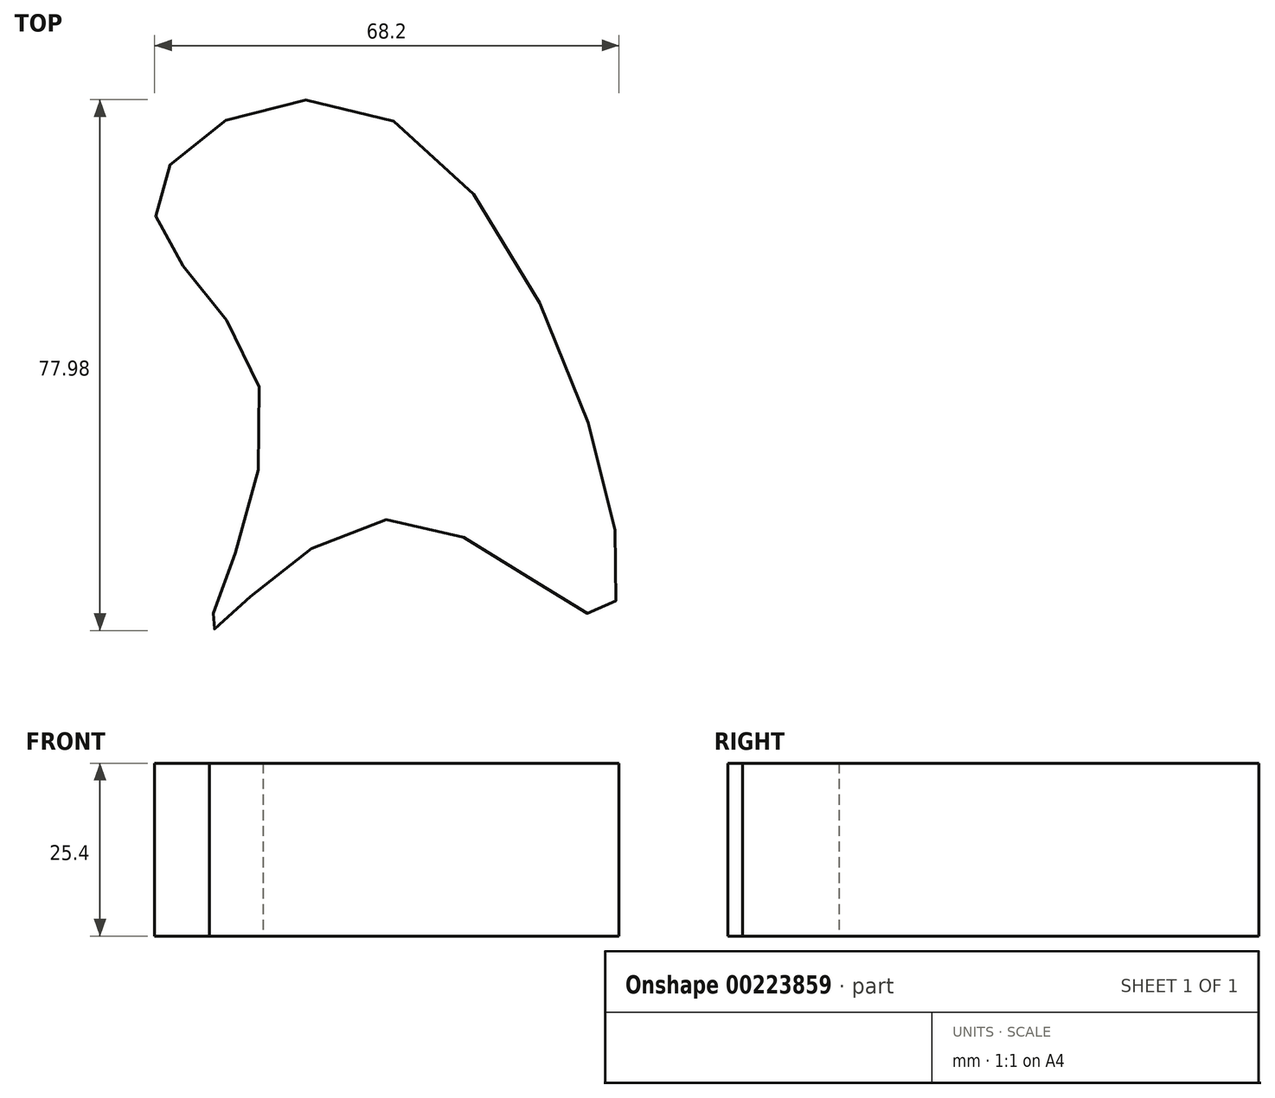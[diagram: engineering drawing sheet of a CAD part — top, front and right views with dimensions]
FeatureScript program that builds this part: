
annotation { "Feature Type Name" : "Feature", "Feature Type Description" : "" }
export const myFeature = defineFeature(function(context is Context, id is Id, definition is map)
    precondition{}
    {
        {
            var Q0;
            Q0=qCreatedBy(makeId("Top.planeOp"),FACE);
            var sketch = newSketch(context, id + "F0", { "sketchPlane" : qUnion([Q0])});
            skFitSpline(sketch, "E0", {"points": [v(0, 40.57) * mm, v(-35.01, 29.09) * mm, v(-19.45, 0) * mm, v(-26.86, -34.27) * mm, v(0, -17.97) * mm, v(31.68, -31.68) * mm, v(0, 40.57) * mm]});
            skSolve(sketch);
        }
        {
            var Q0;
            Q0 = qSketchRegion(id + "F0", true);
            extrude(context, id + "F1", {"entities" : qUnion([Q0]), "depth" : 25.4 * mm});
        }
    });
